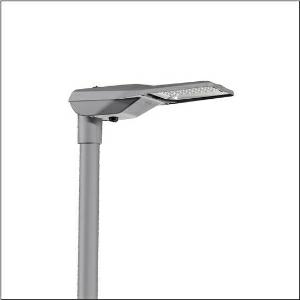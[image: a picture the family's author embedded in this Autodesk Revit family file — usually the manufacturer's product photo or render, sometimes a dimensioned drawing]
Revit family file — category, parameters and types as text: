
# Revit family: streetlight_sl_21_mini___st0_8a_5xe2c33t08gb_9409
name_source: partatom
category: Lighting Fixtures
units: mm (PartAtom-declared; Revit-internal decimal feet)

## family parameters
Cut with Voids When Loaded = No
Host = Face
Light Source = No
Part Type = Normal
Room Calculation Point = No
Round Connector Dimension = Use Diameter
Shared = No

## types (1)
- --- (1 x LED, 5940 lm, 40.4 W, 3000K)
    Apparent Load = 40 VA
    CIE Flux Codes = 38 75 97 100 100
    Color Rendering = 70
    Color Temperature = 3000K
    Default Elevation = 1800 mm
    Description = Streetlight SL 21 mini, mast luminaire, primary light control with lens, of PMMA, primary optical cover: cover, of toughened safety glass, transparent, light distribution: ST0.8a, light emission: direct distribution, primary light characteristic: asymmetric, installation type: side-entry, post-top, LED, High Power LED, rated luminous flux: 5.940lm, luminous efficacy: 147lm/W, light colour: 730, colour temperature: 3000K, control gear: D4i, control: overheat protection, constant luminous flux control, time-dependent luminous flux control, flexible luminous flux parameterisation, pre-setting: logarithmic dimming characteristic, mains connection: 220..240V, AC, 50/60Hz, start of lifetime: 40W, end of service life: 41W, reduction: 19W, luminaire housing, of diecast aluminium, powder-coated, SITECO metallic grey (DB 702S), corrosivity category C5 high according to DIN EN ISO 12944, please order mast flange separately, inclination adjustable: 0°, 5°, 10°, 15°, sealing non-destructively replaceable, multi-level sealing system, length: 628mm, width: 235mm, height: 110mm, mast flange for spigot size: 42mm (side-entry): 5XC10008XM4, 60/48mm (side-entry/post-top): 5XC10108XM2, 76/60mm (side-entry/post-top): 5XC10108XM1, mounting height: 4..8m, Smart Interface below and above, protection rating (complete): IP66, insulation class (complete): insulation class II (safety insulation), certification: CE, ENEC, ENEC+, VDE, impact resistance: IK10, permissible operating ambient temperature for outdoor applications: -40..+50°C, standard-compliant lighting for roads and squares, packaging unit: 1 piece

Light Distribution: ST0.8a
    Height = 110 mm
    Lamp = 1 x LED
    Lamp Light Flux = 5940 lm
    Lamp Power = 40.4 W
    Lamp count = 1
    Length = 625 mm
    Luminous efficacy = 147 lm/W
    Manufacturer = Siteco
    ModVariant = No
    Model = 5XE2C33T08GB
    Number of Poles = 1
    OnlyDefault = Yes
    Power Factor = 1
    Product Name = Streetlight SL 21 mini | ST0.8a
    Product group = mast luminaire | pylon top
    ProductGroupID = 6100
    Protection Class = Protection class II
    Protection Degree = IP 66
    RLX_Detail_Level = 1
    RLX_Emergency_Light_Flux = 0 lm
    RLX_Emergency_Type = 0
    RLX_Emergency_Type_DB = No
    RlxData = <blob elided: 26393 chars, md5=2fbc5ff6>
    Socket = socket
    Standby Power = 0 W
    System Light Flux = 5940 lm
    System Power = 40 W
    Type Comments = factory setting: luminous flux: 100 % | dim-lin: 254 | 812 mA
    Type Image = l_1003514.jpg
    URL = http://relux.com
    VarID = @adj_182881
    Voltage = 0 V
    Weight = 0.00 kg
    Width = 234 mm

## geometry (parser evidence)
native form markers: Blend x4, Sweep x10
no freeform markers — native parametric forms only
